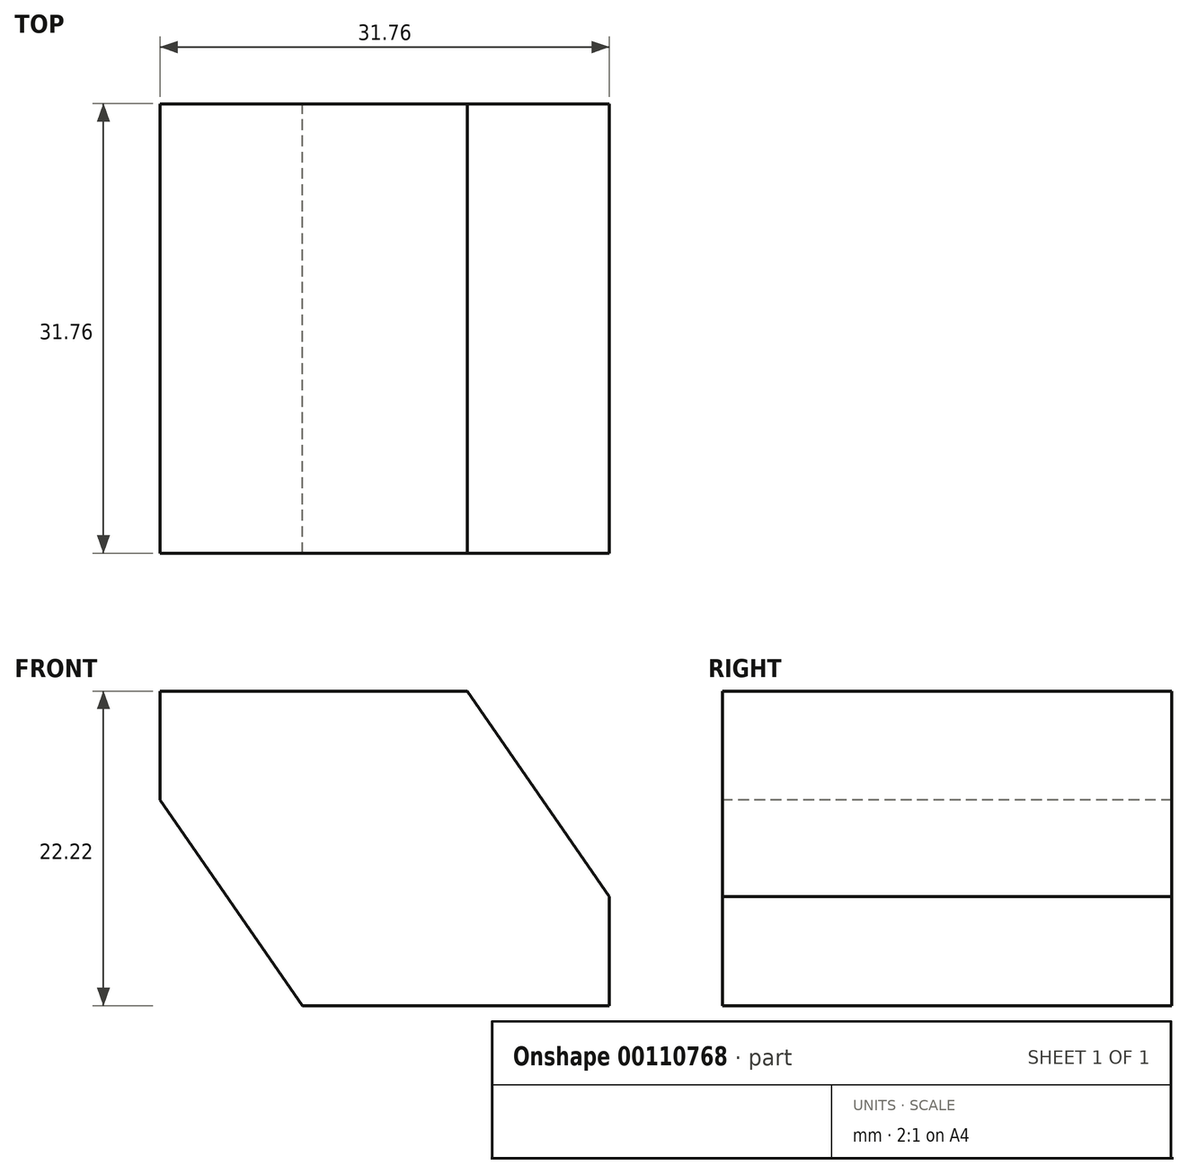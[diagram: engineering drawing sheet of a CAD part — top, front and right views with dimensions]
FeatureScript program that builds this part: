
annotation { "Feature Type Name" : "Feature", "Feature Type Description" : "" }
export const myFeature = defineFeature(function(context is Context, id is Id, definition is map)
    precondition{}
    {
        {
            var Q0;
            Q0=qCreatedBy(makeId("Front.planeOp"),FACE);
            var sketch = newSketch(context, id + "F0", { "sketchPlane" : qUnion([Q0])});
            skLineSegment(sketch, "E0.bottom", {"start": v(15.88, -11.11) * mm, "end": v(-15.88, -11.11) * mm});
            skLineSegment(sketch, "E0.top", {"start": v(15.87, 11.11) * mm, "end": v(-15.87, 11.11) * mm});
            skLineSegment(sketch, "E0.left", {"start": v(15.88, -11.11) * mm, "end": v(15.88, 11.11) * mm});
            skLineSegment(sketch, "E0.right", {"start": v(-15.88, -11.11) * mm, "end": v(-15.88, 11.11) * mm});
            skPoint(sketch, "E0.middle", {"position": v(0, 0) * mm});
            skLineSegment(sketch, "E1", {"start": v(0, -18.78) * mm, "end": v(0, 18.22) * mm, "construction": true});
            skPoint(sketch, "E1.endSnap0", {"position": v(0, 11.11) * mm});
            skSolve(sketch);
        }
        {
            var Q0;
            Q0 = qSketchRegion(id + "F0", true);
            extrude(context, id + "F1", {"entities" : qUnion([Q0]), "depth" : 15.88 * mm, "hasSecondDirection" : true, "secondDirectionOppositeDirection" : true, "secondDirectionDepth" : 15.88 * mm});
        }
        {
            var Q0;
            Q0=qCreatedBy(makeId("Front.planeOp"),FACE);
            var sketch = newSketch(context, id + "F2", { "sketchPlane" : qUnion([Q0])});
            skCircle(sketch, "E2", {"center": v(0, 0) * mm, "radius": 11.11 * mm, "construction": true});
            skLineSegment(sketch, "E3", {"start": v(5.83, 11.11) * mm, "end": v(21.2, -11.11) * mm});
            skLineSegment(sketch, "E4", {"start": v(-5.83, -11.11) * mm, "end": v(-21.2, 11.11) * mm});
            skLineSegment(sketch, "E5.0.0", {"start": v(-21.2, -11.11) * mm, "end": v(-5.83, -11.11) * mm});
            skLineSegment(sketch, "E5.0.2", {"start": v(21.2, 11.11) * mm, "end": v(5.83, 11.11) * mm});
            skPoint(sketch, "E6.orphan", {"position": v(-15.88, 11.11) * mm});
            skPoint(sketch, "E7.orphan", {"position": v(15.88, -11.11) * mm});
            skLineSegment(sketch, "E8", {"start": v(-21.2, 11.11) * mm, "end": v(-21.2, -11.11) * mm});
            skLineSegment(sketch, "E9", {"start": v(21.2, -11.11) * mm, "end": v(21.2, 11.11) * mm});
            skSolve(sketch);
        }
        {
            var Q0;
            Q0 = qSketchRegion(id + "F2", true);
            var Q1;
            Q1 = qConstructionFilter(qBodyType(qCreatedBy(id + "F2" ,EDGE), BodyType.WIRE), ConstructionObject.NO);
            extrude(context, id + "F3", {"entities" : qUnion([Q0]), "operationType" : NewBodyOperationType.REMOVE, "surfaceEntities" : qUnion([Q1]), "endBound" : BoundingType.THROUGH_ALL, "depth" : 25.4 * mm, "hasSecondDirection" : true, "secondDirectionBound" : SecondDirectionBoundingType.THROUGH_ALL, "secondDirectionOppositeDirection" : true, "secondDirectionDepth" : 25.4 * mm});
        }
    });
